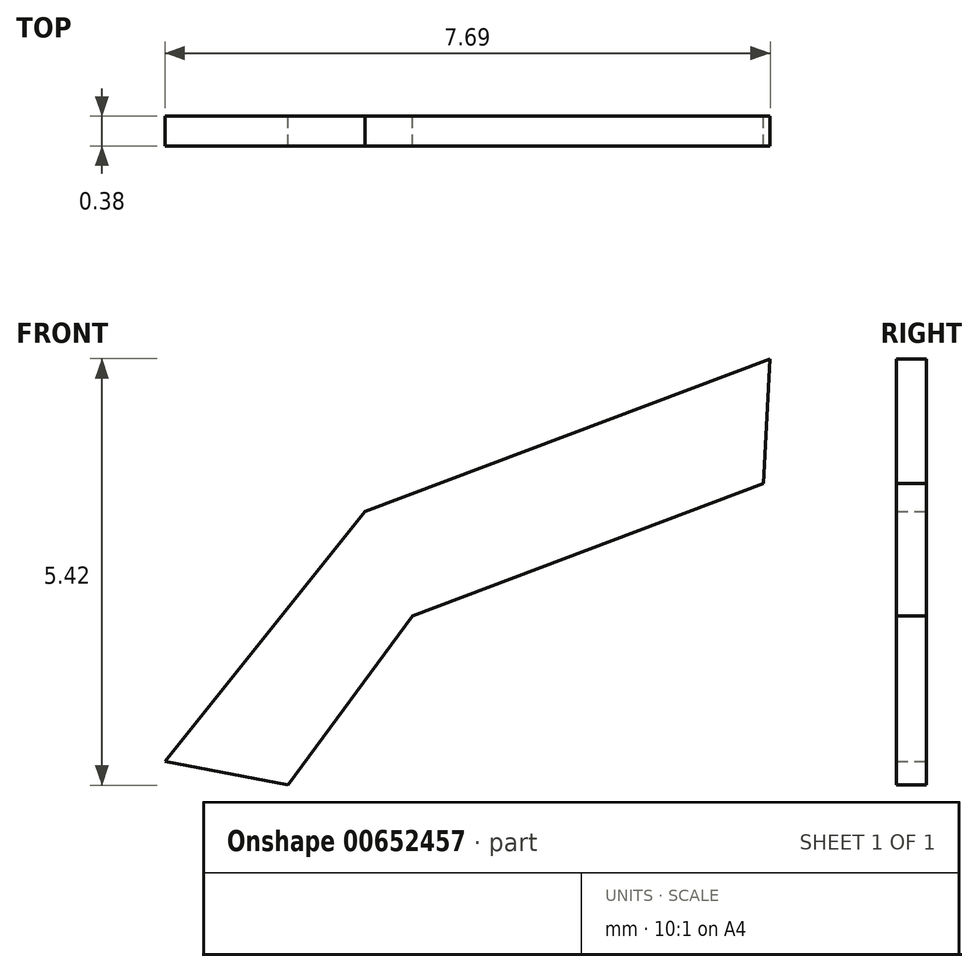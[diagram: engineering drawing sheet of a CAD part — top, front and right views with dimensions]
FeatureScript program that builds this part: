
annotation { "Feature Type Name" : "Feature", "Feature Type Description" : "" }
export const myFeature = defineFeature(function(context is Context, id is Id, definition is map)
    precondition{}
    {
        {
            var Q0;
            Q0=qCreatedBy(makeId("Front.planeOp"),FACE);
            var sketch = newSketch(context, id + "F0", { "sketchPlane" : qUnion([Q0])});
            skLineSegment(sketch, "E0", {"start": v(-7.65, 0.2) * mm, "end": v(-5.1, 3.38) * mm});
            skLineSegment(sketch, "E1", {"start": v(-5.1, 3.38) * mm, "end": v(0.04, 5.32) * mm});
            skLineSegment(sketch, "E2", {"start": v(-0.05, 3.73) * mm, "end": v(-4.5, 2.05) * mm});
            skLineSegment(sketch, "E3", {"start": v(-4.5, 2.05) * mm, "end": v(-6.09, -0.1) * mm});
            skLineSegment(sketch, "E4", {"start": v(-7.65, 0.2) * mm, "end": v(-6.09, -0.1) * mm});
            skLineSegment(sketch, "E5", {"start": v(0.04, 5.32) * mm, "end": v(-0.05, 3.73) * mm});
            skSolve(sketch);
        }
        {
            var Q0;
            Q0 = qSketchRegion(id + "F0", true);
            extrude(context, id + "F1", {"entities" : qUnion([Q0]), "endBound" : BoundingType.SYMMETRIC, "depth" : 0.38 * mm, "offsetDistance" : 25.4 * mm});
        }
    });
